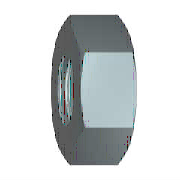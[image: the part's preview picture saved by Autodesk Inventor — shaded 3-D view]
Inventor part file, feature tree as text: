
AUTODESK INVENTOR PART (.ipt)
format: ipt  version: 2024 (Build 280153000, 153)  size: 170,496 bytes
history: native  units: mm (DEFAULTED — no unit token found)
features: chamfer x1, hole x1, other x1, plane x1
ambient origin geometry x7: Origin, YZ Plane, XZ Plane, X Axis, Y Axis, Z Axis, Center Point
bodies: Solid1 (feature_tree), Body (feature_tree)
feature tree (4):
  chamfer  "Chamfer1"  Distance=18.475209mm
  hole  "Thread"  [1 undecoded]
  other  "Work Axis1"
  plane  "Work Plane1"
note: 1 required parameter value undecoded (feature->parameter linkage not recoverable at this tier; creation-order binding heuristic only, values carry confidence <= 0.55)
